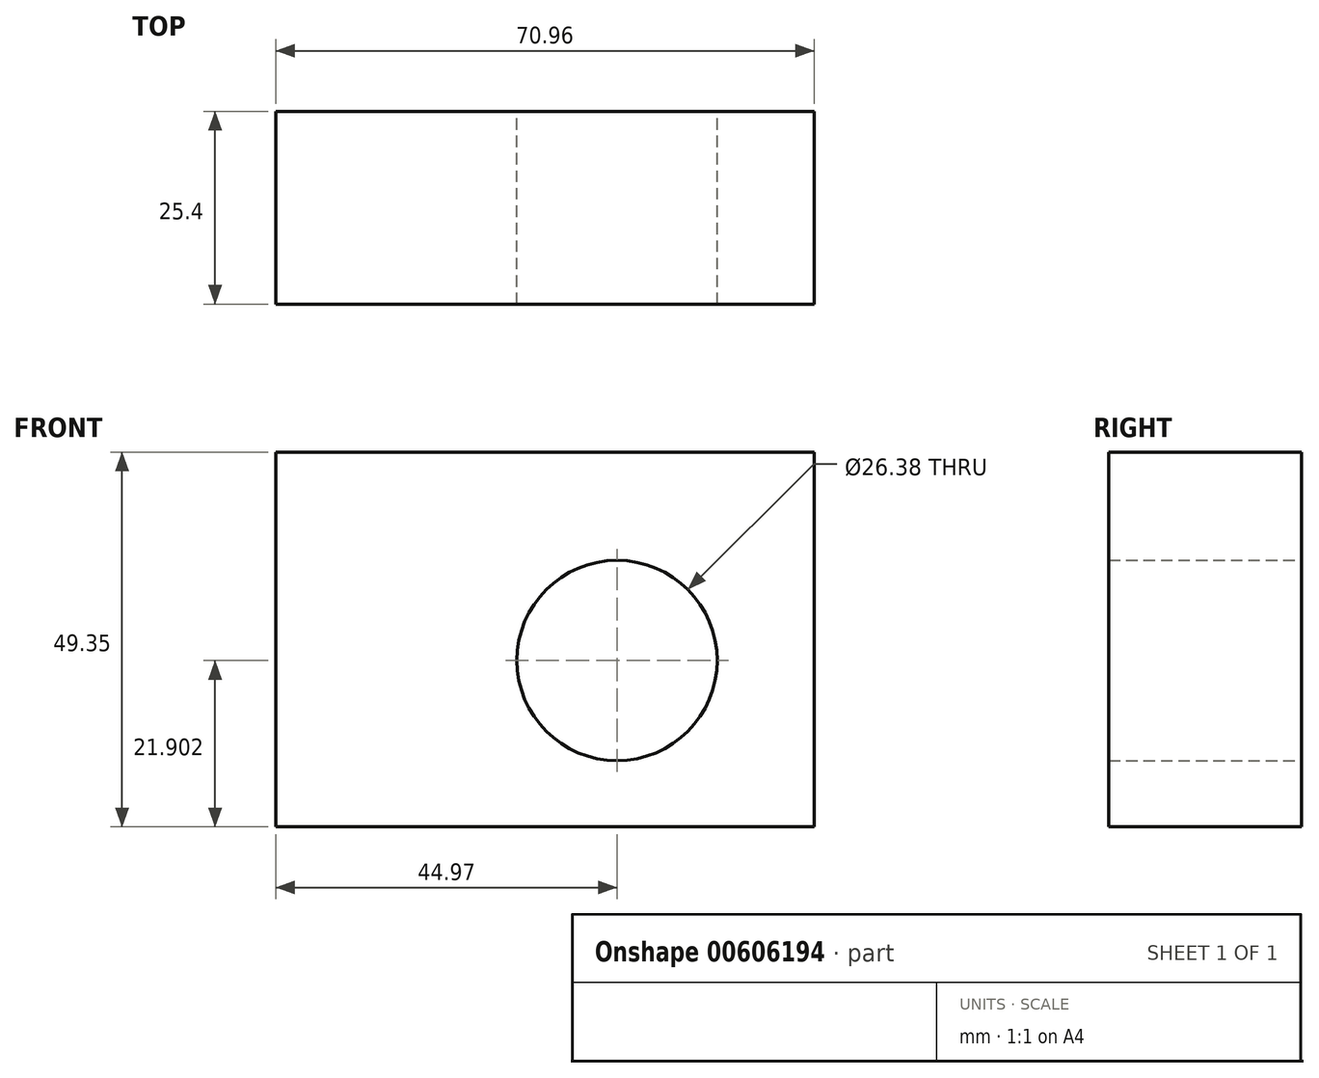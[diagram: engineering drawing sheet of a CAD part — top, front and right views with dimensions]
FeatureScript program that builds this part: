
annotation { "Feature Type Name" : "Feature", "Feature Type Description" : "" }
export const myFeature = defineFeature(function(context is Context, id is Id, definition is map)
    precondition{}
    {
        {
            var Q0;
            Q0=qCreatedBy(makeId("Front.planeOp"),FACE);
            var sketch = newSketch(context, id + "F0", { "sketchPlane" : qUnion([Q0])});
            skLineSegment(sketch, "E0.bottom", {"start": v(-28.18, 13.87) * mm, "end": v(42.78, 13.87) * mm});
            skLineSegment(sketch, "E0.top", {"start": v(-28.18, -35.48) * mm, "end": v(42.78, -35.48) * mm});
            skLineSegment(sketch, "E0.left", {"start": v(-28.18, 13.87) * mm, "end": v(-28.18, -35.48) * mm});
            skLineSegment(sketch, "E0.right", {"start": v(42.78, 13.87) * mm, "end": v(42.78, -35.48) * mm});
            skCircle(sketch, "E1", {"center": v(16.8, -13.58) * mm, "radius": 13.2 * mm});
            skSolve(sketch);
        }
        {
            var Q0;
            Q0=makeQuery(id+"F0.imprint","IMPRINT",FACE,{"disambiguationData":[TD([[makeQuery(id+"F0.imprint","IMPRINT",EDGE,{"derivedFrom":sQuery(id+"F0.wireOp",EDGE,"E0.bottom")}),-1.0]])]});
            extrude(context, id + "F1", {"entities" : qUnion([Q0]), "depth" : 25.4 * mm, "offsetDistance" : 25.4 * mm});
        }
    });
